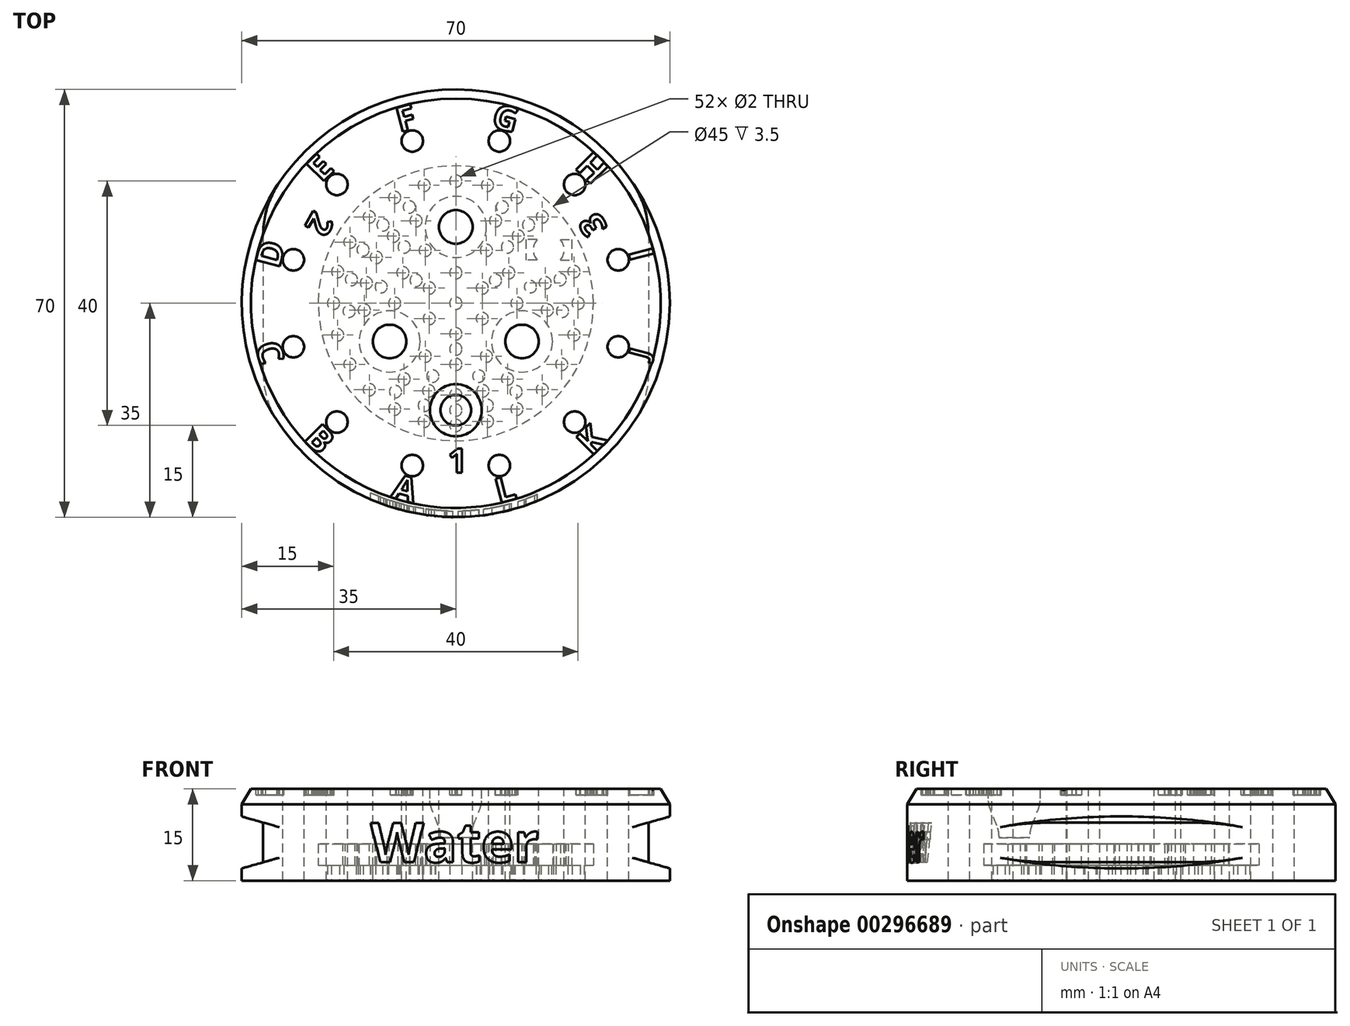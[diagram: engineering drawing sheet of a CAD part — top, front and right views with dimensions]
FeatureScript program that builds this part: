
annotation { "Feature Type Name" : "Feature", "Feature Type Description" : "" }
export const myFeature = defineFeature(function(context is Context, id is Id, definition is map)
    precondition{}
    {
        {
            var Q0;
            Q0=qCreatedBy(makeId("Top.planeOp"),FACE);
            var sketch = newSketch(context, id + "F0", { "sketchPlane" : qUnion([Q0])});
            skCircle(sketch, "E0", {"center": v(0, 0) * mm, "radius": 35 * mm});
            skSolve(sketch);
        }
        {
            var Q0;
            Q0=qSketchRegion(id+"F0",true);
            extrude(context, id + "F1", {"entities" : qUnion([Q0]), "depth" : 15 * mm});
        }
        {
            var Q0;
            Q0=qCreatedBy(makeId("Front.planeOp"),FACE);
            var sketch = newSketch(context, id + "F2", { "sketchPlane" : qUnion([Q0])});
            skText(sketch, "E1", { "text": "Water", "fontName": "OpenSans-Bold.ttf"});
            const initialGuessF2  = {"E1": [-0.01396, 0.003, 1, 0, 0.0065]};
            skSetInitialGuess(sketch, initialGuessF2);
            skSolve(sketch);
        }
        {
            var Q0;
            Q0=qSketchRegion(id+"F2",true);
            var Q1;
            Q1=makeQuery(id+"F1.opExtrude","SWEPT_FACE",FACE,{"disambiguationData":[OSD([sQuery(id+"F0.wireOp",EDGE,"E0")])]});
            extrude(context, id + "F3", {"entities" : qUnion([Q0]), "operationType" : NewBodyOperationType.REMOVE, "endBound" : BoundingType.THROUGH_ALL, "endBoundEntityFace" : qUnion([Q1]), "depth" : 25 * mm});
        }
        {
            var Q0;
            Q0=makeQuery(id+"F1.opExtrude","CAP_FACE",FACE,{"disambiguationData":[OSD([sQuery(id+"F0.wireOp",EDGE,"E0")])],"isStart":false});
            var sketch = newSketch(context, id + "F4", { "sketchPlane" : qUnion([Q0])});
            skCircle(sketch, "E2", {"center": v(0, 0) * mm, "radius": 34 * mm});
            skSolve(sketch);
        }
        {
            var Q0;
            Q0=qSketchRegion(id+"F4",true);
            var Q1;
            Q1=makeQuery(id+"F1.opExtrude","CAP_FACE",FACE,{"disambiguationData":[OSD([sQuery(id+"F0.wireOp",EDGE,"E0")])],"isStart":true});
            extrude(context, id + "F5", {"entities" : qUnion([Q0]), "operationType" : NewBodyOperationType.ADD, "endBound" : BoundingType.UP_TO_SURFACE, "oppositeDirection" : true, "endBoundEntityFace" : qUnion([Q1]), "depth" : 25 * mm});
        }
        {
            var Q0;
            Q0=qCreatedBy(makeId("Front.planeOp"),FACE);
            var sketch = newSketch(context, id + "F6", { "sketchPlane" : qUnion([Q0])});
            skLineSegment(sketch, "E3", {"start": v(-35, 10.5) * mm, "end": v(-35, 2) * mm});
            skLineSegment(sketch, "E4", {"start": v(-35, 2) * mm, "end": v(-31.5, 3) * mm});
            skLineSegment(sketch, "E5", {"start": v(-31.5, 3) * mm, "end": v(-31.5, 9.5) * mm});
            skLineSegment(sketch, "E6", {"start": v(-31.5, 9.5) * mm, "end": v(-35, 10.5) * mm});
            skLineSegment(sketch, "E7.MirrorCS", {"start": v(35, 10.5) * mm, "end": v(35, 2) * mm});
            skLineSegment(sketch, "E8.MirrorCS", {"start": v(31.5, 9.5) * mm, "end": v(35, 10.5) * mm});
            skLineSegment(sketch, "E9.MirrorCS", {"start": v(35, 2) * mm, "end": v(31.5, 3) * mm});
            skLineSegment(sketch, "E10.MirrorCS", {"start": v(31.5, 3) * mm, "end": v(31.5, 9.5) * mm});
            skSolve(sketch);
        }
        {
            var Q0;
            Q0=qSketchRegion(id+"F6",true);
            extrude(context, id + "F7", {"entities" : qUnion([Q0]), "operationType" : NewBodyOperationType.REMOVE, "endBound" : BoundingType.THROUGH_ALL, "oppositeDirection" : true, "depth" : 25 * mm, "hasSecondDirection" : true, "secondDirectionBound" : SecondDirectionBoundingType.THROUGH_ALL, "secondDirectionOppositeDirection" : false, "secondDirectionDepth" : 25 * mm});
        }
        {
            var Q0;
            {var subQ0=sQuery(id+"F0.wireOp",EDGE,"E0");Q0=makeQuery(id+"F7.boolean.opBoolean","INTERSECT",EDGE,{"disambiguationData":[OD(0.0)],"derivedFrom":[makeQuery(id+"F3.boolean.opBoolean","SPLIT",FACE,{"disambiguationData":[TD([makeQuery(id+"F1.opExtrude","CAP_FACE",FACE,{"disambiguationData":[OSD([subQ0])],"isStart":true})])],"derivedFrom":makeQuery(id+"F1.opExtrude","SWEPT_FACE",FACE,{"disambiguationData":[OSD([subQ0])]})}),makeQuery(id+"F7.opExtrude","SWEPT_FACE",FACE,{"disambiguationData":[OSD([sQuery(id+"F6.wireOp",EDGE,"E5")])]})]});}
            var Q1;
            {var subQ0=sQuery(id+"F0.wireOp",EDGE,"E0");Q1=makeQuery(id+"F7.boolean.opBoolean","INTERSECT",EDGE,{"disambiguationData":[OD(0.0)],"derivedFrom":[makeQuery(id+"F3.boolean.opBoolean","SPLIT",FACE,{"disambiguationData":[TD([makeQuery(id+"F1.opExtrude","CAP_FACE",FACE,{"disambiguationData":[OSD([subQ0])],"isStart":true})])],"derivedFrom":makeQuery(id+"F1.opExtrude","SWEPT_FACE",FACE,{"disambiguationData":[OSD([subQ0])]})}),makeQuery(id+"F7.opExtrude","SWEPT_FACE",FACE,{"disambiguationData":[OSD([sQuery(id+"F6.wireOp",EDGE,"E10.MirrorCS")])]})]});}
            var Q2;
            {var subQ0=sQuery(id+"F0.wireOp",EDGE,"E0");Q2=makeQuery(id+"F7.boolean.opBoolean","INTERSECT",EDGE,{"disambiguationData":[OD(1.0)],"derivedFrom":[makeQuery(id+"F3.boolean.opBoolean","SPLIT",FACE,{"disambiguationData":[TD([makeQuery(id+"F1.opExtrude","CAP_FACE",FACE,{"disambiguationData":[OSD([subQ0])],"isStart":true})])],"derivedFrom":makeQuery(id+"F1.opExtrude","SWEPT_FACE",FACE,{"disambiguationData":[OSD([subQ0])]})}),makeQuery(id+"F7.opExtrude","SWEPT_FACE",FACE,{"disambiguationData":[OSD([sQuery(id+"F6.wireOp",EDGE,"E10.MirrorCS")])]})]});}
            var Q3;
            {var subQ0=sQuery(id+"F0.wireOp",EDGE,"E0");Q3=makeQuery(id+"F7.boolean.opBoolean","INTERSECT",EDGE,{"disambiguationData":[OD(1.0)],"derivedFrom":[makeQuery(id+"F3.boolean.opBoolean","SPLIT",FACE,{"disambiguationData":[TD([makeQuery(id+"F1.opExtrude","CAP_FACE",FACE,{"disambiguationData":[OSD([subQ0])],"isStart":true})])],"derivedFrom":makeQuery(id+"F1.opExtrude","SWEPT_FACE",FACE,{"disambiguationData":[OSD([subQ0])]})}),makeQuery(id+"F7.opExtrude","SWEPT_FACE",FACE,{"disambiguationData":[OSD([sQuery(id+"F6.wireOp",EDGE,"E5")])]})]});}
            fillet(context, id + "F8", {"entities" : qUnion([Q0, Q1, Q2, Q3]), "radius" : 15 * mm, "tangentPropagation" : true, "allowEdgeOverflow" : false});
        }
        {
            var Q0;
            Q0=makeQuery(id+"F1.opExtrude","CAP_FACE",FACE,{"disambiguationData":[OSD([sQuery(id+"F0.wireOp",EDGE,"E0")])],"isStart":false});
            var sketch = newSketch(context, id + "F9", { "sketchPlane" : qUnion([Q0])});
            skCircle(sketch, "E11", {"center": v(0, 12.5) * mm, "radius": 2.75 * mm});
            skCircle(sketch, "E12.1.0", {"center": v(-10.83, -6.25) * mm, "radius": 2.75 * mm});
            skCircle(sketch, "E12.2.0", {"center": v(10.83, -6.25) * mm, "radius": 2.75 * mm});
            skPoint(sketch, "E12.center", {"position": v(0, 0) * mm});
            skCircle(sketch, "E13", {"center": v(0, 0) * mm, "radius": 12.5 * mm, "construction": true});
            skSolve(sketch);
        }
        {
            var Q0;
            Q0=qSketchRegion(id+"F9",true);
            extrude(context, id + "F10", {"entities" : qUnion([Q0]), "operationType" : NewBodyOperationType.REMOVE, "endBound" : BoundingType.THROUGH_ALL, "oppositeDirection" : true, "depth" : 25 * mm});
        }
        {
            var Q0;
            Q0=makeQuery(id+"F1.opExtrude","CAP_FACE",FACE,{"disambiguationData":[OSD([sQuery(id+"F0.wireOp",EDGE,"E0")])],"isStart":false});
            var sketch = newSketch(context, id + "F11", { "sketchPlane" : qUnion([Q0])});
            skCircle(sketch, "E14", {"center": v(0, -17.5) * mm, "radius": 2.5 * mm});
            skCircle(sketch, "E15", {"center": v(0, 0) * mm, "radius": 17.5 * mm, "construction": true});
            skSolve(sketch);
        }
        {
            var Q0;
            Q0=qSketchRegion(id+"F11",true);
            extrude(context, id + "F12", {"entities" : qUnion([Q0]), "operationType" : NewBodyOperationType.REMOVE, "endBound" : BoundingType.THROUGH_ALL, "oppositeDirection" : true, "depth" : 25 * mm});
        }
        {
            var Q0;
            Q0=makeQuery(id+"F1.opExtrude","CAP_FACE",FACE,{"disambiguationData":[OSD([sQuery(id+"F0.wireOp",EDGE,"E0")])],"isStart":false});
            var sketch = newSketch(context, id + "F13", { "sketchPlane" : qUnion([Q0])});
            skCircle(sketch, "E16", {"center": v(0, -17.5) * mm, "radius": 4.25 * mm});
            skSolve(sketch);
        }
        {
            var Q0;
            Q0=qSketchRegion(id+"F13",true);
            extrude(context, id + "F14", {"entities" : qUnion([Q0]), "operationType" : NewBodyOperationType.REMOVE, "oppositeDirection" : true, "depth" : 7.5 * mm});
        }
        {
            var Q0;
            Q0=makeQuery(id+"F14.boolean.opBoolean","COPY",EDGE,{"derivedFrom":makeQuery(id+"F14.opExtrude","CAP_EDGE",EDGE,{"disambiguationData":[OSD([sQuery(id+"F13.wireOp",EDGE,"E16")])],"isStart":false})});
            chamfer(context, id + "F15", {"entities" : qUnion([Q0]), "chamferType" : ChamferType.TWO_OFFSETS, "width1" : 5 * mm, "oppositeDirection" : true, "width2" : 2 * mm, "tangentPropagation" : true});
        }
        {
            var Q0;
            {var subQ0=sQuery(id+"F13.wireOp",EDGE,"E16");Q0=makeQuery(id+"F15.opChamfer","BLEND_EDGE",EDGE,{"blendedFrom":[makeQuery(id+"F14.boolean.opBoolean","COPY",EDGE,{"derivedFrom":makeQuery(id+"F14.opExtrude","CAP_EDGE",EDGE,{"disambiguationData":[OSD([subQ0])],"isStart":false})}),makeQuery(id+"F14.boolean.opBoolean","COPY",FACE,{"derivedFrom":makeQuery(id+"F14.opExtrude","SWEPT_FACE",FACE,{"disambiguationData":[OSD([subQ0])]})})],"blendedInto":[makeQuery(id+"F14.boolean.opBoolean","COPY",FACE,{"derivedFrom":makeQuery(id+"F14.opExtrude","SWEPT_FACE",FACE,{"disambiguationData":[OSD([subQ0])]})})]});}
            var Q1;
            Q1=makeQuery(id+"F15.opChamfer","BLEND_EDGE",EDGE,{"blendedFrom":[makeQuery(id+"F14.boolean.opBoolean","COPY",EDGE,{"derivedFrom":makeQuery(id+"F14.opExtrude","CAP_EDGE",EDGE,{"disambiguationData":[OSD([sQuery(id+"F13.wireOp",EDGE,"E16")])],"isStart":false})}),makeQuery(id+"F12.boolean.opBoolean","COPY",FACE,{"derivedFrom":makeQuery(id+"F12.opExtrude","SWEPT_FACE",FACE,{"disambiguationData":[OSD([sQuery(id+"F11.wireOp",EDGE,"E14")])]})})],"blendedInto":[makeQuery(id+"F12.boolean.opBoolean","COPY",FACE,{"derivedFrom":makeQuery(id+"F12.opExtrude","SWEPT_FACE",FACE,{"disambiguationData":[OSD([sQuery(id+"F11.wireOp",EDGE,"E14")])]})})]});
            fillet(context, id + "F16", {"entities" : qUnion([Q0, Q1]), "radius" : 5 * mm, "tangentPropagation" : true, "allowEdgeOverflow" : false});
        }
        {
            var Q0;
            Q0=makeQuery(id+"F1.opExtrude","CAP_FACE",FACE,{"disambiguationData":[OSD([sQuery(id+"F0.wireOp",EDGE,"E0")])],"isStart":false});
            var sketch = newSketch(context, id + "F17", { "sketchPlane" : qUnion([Q0])});
            skCircle(sketch, "E17", {"center": v(19.45, 19.45) * mm, "radius": 1.75 * mm});
            skCircle(sketch, "E18", {"center": v(0, 0) * mm, "radius": 27.5 * mm, "construction": true});
            skLineSegment(sketch, "E19", {"start": v(0, 0) * mm, "end": v(19.45, 19.45) * mm, "construction": true});
            skCircle(sketch, "E20.1.1", {"center": v(7.12, 26.56) * mm, "radius": 1.75 * mm});
            skCircle(sketch, "E20.2.1", {"center": v(-7.12, 26.56) * mm, "radius": 1.75 * mm});
            skCircle(sketch, "E20.3.1", {"center": v(-19.45, 19.45) * mm, "radius": 1.75 * mm});
            skCircle(sketch, "E20.4.1", {"center": v(-26.56, 7.12) * mm, "radius": 1.75 * mm});
            skCircle(sketch, "E20.5.1", {"center": v(-26.56, -7.12) * mm, "radius": 1.75 * mm});
            skCircle(sketch, "E20.6.1", {"center": v(-19.45, -19.45) * mm, "radius": 1.75 * mm});
            skCircle(sketch, "E20.7.1", {"center": v(-7.12, -26.56) * mm, "radius": 1.75 * mm});
            skCircle(sketch, "E20.8.1", {"center": v(7.12, -26.56) * mm, "radius": 1.75 * mm});
            skCircle(sketch, "E20.9.1", {"center": v(19.45, -19.45) * mm, "radius": 1.75 * mm});
            skCircle(sketch, "E20.10.1", {"center": v(26.56, -7.12) * mm, "radius": 1.75 * mm});
            skCircle(sketch, "E20.11.1", {"center": v(26.56, 7.12) * mm, "radius": 1.75 * mm});
            skSolve(sketch);
        }
        {
            var Q0;
            Q0=qSketchRegion(id+"F17",true);
            extrude(context, id + "F18", {"entities" : qUnion([Q0]), "operationType" : NewBodyOperationType.REMOVE, "endBound" : BoundingType.THROUGH_ALL, "oppositeDirection" : true, "depth" : 25 * mm});
        }
        {
            var Q0;
            Q0=makeQuery(id+"F1.opExtrude","CAP_EDGE",EDGE,{"disambiguationData":[OSD([sQuery(id+"F0.wireOp",EDGE,"E0")])],"isStart":false});
            chamfer(context, id + "F19", {"entities" : qUnion([Q0]), "chamferType" : ChamferType.TWO_OFFSETS, "width1" : 2.5 * mm, "oppositeDirection" : true, "width2" : 1.5 * mm, "tangentPropagation" : true});
        }
        {
            var Q0;
            Q0=makeQuery(id+"F1.opExtrude","CAP_FACE",FACE,{"disambiguationData":[OSD([sQuery(id+"F0.wireOp",EDGE,"E0")])],"isStart":false});
            var sketch = newSketch(context, id + "F20", { "sketchPlane" : qUnion([Q0])});
            skText(sketch, "E21", { "text": "A", "fontName": "OpenSans-Bold.ttf"});
            skText(sketch, "E22", { "text": "B", "fontName": "OpenSans-Bold.ttf"});
            skText(sketch, "E23", { "text": "C", "fontName": "OpenSans-Bold.ttf"});
            skText(sketch, "E24", { "text": "E", "fontName": "OpenSans-Bold.ttf"});
            skText(sketch, "E25", { "text": "F", "fontName": "OpenSans-Bold.ttf"});
            skText(sketch, "E26", { "text": "G", "fontName": "OpenSans-Bold.ttf"});
            skText(sketch, "E27", { "text": "H", "fontName": "OpenSans-Bold.ttf"});
            skText(sketch, "E28", { "text": "I", "fontName": "OpenSans-Bold.ttf"});
            skText(sketch, "E29", { "text": "J", "fontName": "OpenSans-Bold.ttf"});
            skText(sketch, "E30", { "text": "K", "fontName": "OpenSans-Bold.ttf"});
            skText(sketch, "E31", { "text": "L", "fontName": "OpenSans-Bold.ttf"});
            skText(sketch, "E32", { "text": "D", "fontName": "OpenSans-Bold.ttf"});
            skCircle(sketch, "E33", {"center": v(0, 0) * mm, "radius": 29.38 * mm, "construction": true});
            skText(sketch, "E34", { "text": "1", "fontName": "OpenSans-Bold.ttf"});
            skText(sketch, "E35", { "text": "2", "fontName": "OpenSans-Bold.ttf"});
            skText(sketch, "E36", { "text": "3", "fontName": "OpenSans-Bold.ttf"});
            skCircle(sketch, "E37", {"center": v(0, 0) * mm, "radius": 23.75 * mm, "construction": true});
            const initialGuessF20  = {"E21": [-0.0107, -0.03174, 0.96593, -0.25882, 0.00406], "E22": [-0.025, -0.02228, 0.7071, -0.7071, 0.00406], "E23": [-0.03278, -0.00684, 0.25882, -0.96593, 0.00406], "E24": [-0.0219, 0.01964, 0.7071, 0.7071, 0.00406], "E25": [-0.00914, 0.02796, 0.96593, 0.25882, 0.00406], "E26": [0.00567, 0.0289, 0.96593, -0.25882, 0.00406], "E27": [0.0193, 0.02225, 0.7071, -0.7071, 0.00406], "E28": [0.02815, 0.00844, 0.25882, -0.96593, 0.00406], "E29": [0.0313, -0.00927, 0.25882, 0.96593, 0.00325], "E30": [0.02219, -0.0251, 0.7071, 0.7071, 0.00406], "E31": [0.00703, -0.03273, 0.96593, 0.25882, 0.00406], "E32": [-0.02892, 0.00557, 0.25882, 0.96593, 0.00406], "E34": [-0.00133, -0.02775, 1, 0, 0.004], "E35": [-0.0232, 0.01533, -0.5, -0.86603, 0.004], "E36": [0.02486, 0.01244, -0.5, 0.86603, 0.004]};
            skSetInitialGuess(sketch, initialGuessF20);
            skSolve(sketch);
        }
        {
            var Q0;
            Q0=qSketchRegion(id+"F20",true);
            extrude(context, id + "F21", {"entities" : qUnion([Q0]), "operationType" : NewBodyOperationType.REMOVE, "oppositeDirection" : true, "depth" : 1 * mm});
        }
        {
            var Q0;
            Q0=makeQuery(id+"F1.opExtrude","CAP_FACE",FACE,{"disambiguationData":[OSD([sQuery(id+"F0.wireOp",EDGE,"E0")])],"isStart":true});
            var sketch = newSketch(context, id + "F22", { "sketchPlane" : qUnion([Q0])});
            skCircle(sketch, "E38.0", {"center": v(0, 17.5) * mm, "radius": 2.5 * mm});
            skCircle(sketch, "E38.1", {"center": v(-15.16, -8.75) * mm, "radius": 2.5 * mm});
            skSolve(sketch);
        }
        {
            var Q0;
            Q0=qSketchRegion(id+"F22",true);
            extrude(context, id + "F23", {"entities" : qUnion([Q0]), "operationType" : NewBodyOperationType.ADD, "oppositeDirection" : true, "depth" : 7 * mm});
        }
        {
            var Q0;
            Q0=makeQuery(id+"F23.boolean.opBoolean","MERGE",FACE,{"derivedFrom":[makeQuery(id+"F1.opExtrude","CAP_FACE",FACE,{"disambiguationData":[OSD([sQuery(id+"F0.wireOp",EDGE,"E0")])],"isStart":true}),makeQuery(id+"F23.opExtrude","CAP_FACE",FACE,{"disambiguationData":[OSD([sQuery(id+"F22.wireOp",EDGE,"E38.0")])],"isStart":true}),makeQuery(id+"F23.opExtrude","CAP_FACE",FACE,{"disambiguationData":[OSD([sQuery(id+"F22.wireOp",EDGE,"E38.1")])],"isStart":true})]});
            var sketch = newSketch(context, id + "F24", { "sketchPlane" : qUnion([Q0])});
            skCircle(sketch, "E39", {"center": v(0, 0) * mm, "radius": 22.5 * mm});
            skCircle(sketch, "E40", {"center": v(10.83, 6.25) * mm, "radius": 5 * mm});
            skCircle(sketch, "E41", {"center": v(-10.83, 6.25) * mm, "radius": 5 * mm});
            skCircle(sketch, "E42", {"center": v(0, -12.5) * mm, "radius": 5 * mm});
            skSolve(sketch);
        }
        {
            var Q0;
            Q0=qSketchRegion(id+"F24",true);
            extrude(context, id + "F25", {"entities" : qUnion([Q0]), "operationType" : NewBodyOperationType.REMOVE, "oppositeDirection" : true, "depth" : 6 * mm});
        }
        {
            var Q0;
            Q0=makeQuery(id+"F25.boolean.opBoolean","COPY",FACE,{"derivedFrom":makeQuery(id+"F25.opExtrude","CAP_FACE",FACE,{"disambiguationData":[OSD([sQuery(id+"F24.wireOp",EDGE,"E39"),sQuery(id+"F24.wireOp",EDGE,"E40"),sQuery(id+"F24.wireOp",EDGE,"E41"),sQuery(id+"F24.wireOp",EDGE,"E42")])],"isStart":false})});
            var sketch = newSketch(context, id + "F26", { "sketchPlane" : qUnion([Q0])});
            skCircle(sketch, "E43", {"center": v(0, 0) * mm, "radius": 1 * mm});
            skCircle(sketch, "E44", {"center": v(0, 7.5) * mm, "radius": 1 * mm});
            skCircle(sketch, "E45", {"center": v(3.76, 11.92) * mm, "radius": 1 * mm});
            skCircle(sketch, "E46", {"center": v(-3.76, 11.92) * mm, "radius": 1 * mm});
            skCircle(sketch, "E47", {"center": v(0, 17.5) * mm, "radius": 1 * mm});
            skLineSegment(sketch, "E48", {"start": v(3.76, 11.92) * mm, "end": v(0, 0) * mm, "construction": true});
            skCircle(sketch, "E49.1.0", {"center": v(-6.5, -3.75) * mm, "radius": 1 * mm});
            skCircle(sketch, "E49.1.1", {"center": v(-8.44, -9.22) * mm, "radius": 1 * mm});
            skCircle(sketch, "E49.1.2", {"center": v(-12.2, -2.7) * mm, "radius": 1 * mm});
            skCircle(sketch, "E49.2.0", {"center": v(6.5, -3.75) * mm, "radius": 1 * mm});
            skCircle(sketch, "E49.2.1", {"center": v(12.2, -2.7) * mm, "radius": 1 * mm});
            skCircle(sketch, "E49.2.2", {"center": v(8.44, -9.22) * mm, "radius": 1 * mm});
            skCircle(sketch, "E50.1.0", {"center": v(-5.16, 16.72) * mm, "radius": 1 * mm});
            skCircle(sketch, "E50.2.0", {"center": v(-9.86, 14.46) * mm, "radius": 1 * mm});
            skCircle(sketch, "E50.5.0", {"center": v(-17.45, 1.3) * mm, "radius": 1 * mm});
            skCircle(sketch, "E50.6.0", {"center": v(-17.06, -3.9) * mm, "radius": 1 * mm});
            skCircle(sketch, "E50.7.0", {"center": v(-15.16, -8.75) * mm, "radius": 1 * mm});
            skCircle(sketch, "E50.8.0", {"center": v(-11.9, -12.83) * mm, "radius": 1 * mm});
            skCircle(sketch, "E50.9.0", {"center": v(-7.6, -15.77) * mm, "radius": 1 * mm});
            skCircle(sketch, "E50.12.0", {"center": v(7.6, -15.77) * mm, "radius": 1 * mm});
            skCircle(sketch, "E50.13.0", {"center": v(11.9, -12.83) * mm, "radius": 1 * mm});
            skCircle(sketch, "E50.15.0", {"center": v(17.06, -3.9) * mm, "radius": 1 * mm});
            skCircle(sketch, "E50.16.0", {"center": v(17.45, 1.3) * mm, "radius": 1 * mm});
            skCircle(sketch, "E50.19.0", {"center": v(9.86, 14.46) * mm, "radius": 1 * mm});
            skCircle(sketch, "E50.20.0", {"center": v(5.16, 16.72) * mm, "radius": 1 * mm});
            skSolve(sketch);
        }
        {
            var Q0;
            Q0=qSketchRegion(id+"F26",true);
            var Q1;
            {var subQ0=sQuery(id+"F0.wireOp",EDGE,"E0");Q1=makeQuery(id+"F25.boolean.opBoolean","SPLIT",FACE,{"disambiguationData":[TD([makeQuery(id+"F1.opExtrude","SWEPT_FACE",FACE,{"disambiguationData":[OSD([subQ0])]})])],"derivedFrom":makeQuery(id+"F23.boolean.opBoolean","MERGE",FACE,{"derivedFrom":[makeQuery(id+"F1.opExtrude","CAP_FACE",FACE,{"disambiguationData":[OSD([subQ0])],"isStart":true}),makeQuery(id+"F23.opExtrude","CAP_FACE",FACE,{"disambiguationData":[OSD([sQuery(id+"F22.wireOp",EDGE,"E38.0")])],"isStart":true}),makeQuery(id+"F23.opExtrude","CAP_FACE",FACE,{"disambiguationData":[OSD([sQuery(id+"F22.wireOp",EDGE,"E38.1")])],"isStart":true})]})});}
            extrude(context, id + "F27", {"entities" : qUnion([Q0]), "operationType" : NewBodyOperationType.ADD, "endBound" : BoundingType.UP_TO_SURFACE, "endBoundEntityFace" : qUnion([Q1]), "depth" : 25 * mm});
        }
        {
            var Q0;
            {var subQ0=sQuery(id+"F0.wireOp",EDGE,"E0");Q0=makeQuery(id+"F25.boolean.opBoolean","SPLIT",FACE,{"disambiguationData":[TD([makeQuery(id+"F1.opExtrude","SWEPT_FACE",FACE,{"disambiguationData":[OSD([subQ0])]})])],"derivedFrom":makeQuery(id+"F23.boolean.opBoolean","MERGE",FACE,{"derivedFrom":[makeQuery(id+"F1.opExtrude","CAP_FACE",FACE,{"disambiguationData":[OSD([subQ0])],"isStart":true}),makeQuery(id+"F23.opExtrude","CAP_FACE",FACE,{"disambiguationData":[OSD([sQuery(id+"F22.wireOp",EDGE,"E38.0")])],"isStart":true}),makeQuery(id+"F23.opExtrude","CAP_FACE",FACE,{"disambiguationData":[OSD([sQuery(id+"F22.wireOp",EDGE,"E38.1")])],"isStart":true})]})});}
            var sketch = newSketch(context, id + "F28", { "sketchPlane" : qUnion([Q0])});
            skCircle(sketch, "E51.0", {"center": v(0, 0) * mm, "radius": 22.5 * mm});
            skCircle(sketch, "E52.0", {"center": v(-10.83, 6.25) * mm, "radius": 2.75 * mm});
            skCircle(sketch, "E52.1", {"center": v(10.83, 6.25) * mm, "radius": 2.75 * mm});
            skCircle(sketch, "E52.2", {"center": v(0, -12.5) * mm, "radius": 2.75 * mm});
            skSolve(sketch);
        }
        {
            var Q0;
            Q0=qSketchRegion(id+"F28",true);
            extrude(context, id + "F29", {"entities" : qUnion([Q0]), "operationType" : NewBodyOperationType.ADD, "oppositeDirection" : true, "depth" : 2.5 * mm});
        }
        {
            var Q0;
            {var subQ0=sQuery(id+"F0.wireOp",EDGE,"E0");var subQ1=makeQuery(id+"F23.boolean.opBoolean","MERGE",FACE,{"derivedFrom":[makeQuery(id+"F1.opExtrude","CAP_FACE",FACE,{"disambiguationData":[OSD([subQ0])],"isStart":true}),makeQuery(id+"F23.opExtrude","CAP_FACE",FACE,{"disambiguationData":[OSD([sQuery(id+"F22.wireOp",EDGE,"E38.0")])],"isStart":true}),makeQuery(id+"F23.opExtrude","CAP_FACE",FACE,{"disambiguationData":[OSD([sQuery(id+"F22.wireOp",EDGE,"E38.1")])],"isStart":true})]});Q0=makeQuery(id+"F29.boolean.opBoolean","MERGE",FACE,{"derivedFrom":[makeQuery(id+"F25.boolean.opBoolean","SPLIT",FACE,{"disambiguationData":[TD([makeQuery(id+"F1.opExtrude","SWEPT_FACE",FACE,{"disambiguationData":[OSD([subQ0])]})])],"derivedFrom":subQ1}),makeQuery(id+"F25.boolean.opBoolean","SPLIT",FACE,{"disambiguationData":[TD([makeQuery(id+"F10.boolean.opBoolean","COPY",FACE,{"derivedFrom":makeQuery(id+"F10.opExtrude","SWEPT_FACE",FACE,{"disambiguationData":[OSD([sQuery(id+"F9.wireOp",EDGE,"E11")])]})})])],"derivedFrom":subQ1}),makeQuery(id+"F25.boolean.opBoolean","SPLIT",FACE,{"disambiguationData":[TD([makeQuery(id+"F10.boolean.opBoolean","COPY",FACE,{"derivedFrom":makeQuery(id+"F10.opExtrude","SWEPT_FACE",FACE,{"disambiguationData":[OSD([sQuery(id+"F9.wireOp",EDGE,"E12.1.0")])]})})])],"derivedFrom":subQ1}),makeQuery(id+"F25.boolean.opBoolean","SPLIT",FACE,{"disambiguationData":[TD([makeQuery(id+"F10.boolean.opBoolean","COPY",FACE,{"derivedFrom":makeQuery(id+"F10.opExtrude","SWEPT_FACE",FACE,{"disambiguationData":[OSD([sQuery(id+"F9.wireOp",EDGE,"E12.2.0")])]})})])],"derivedFrom":subQ1}),makeQuery(id+"F27.opExtrude","CAP_FACE",FACE,{"disambiguationData":[OSD([sQuery(id+"F26.wireOp",EDGE,"E43")])],"isStart":false}),makeQuery(id+"F27.opExtrude","CAP_FACE",FACE,{"disambiguationData":[OSD([sQuery(id+"F26.wireOp",EDGE,"E44")])],"isStart":false}),makeQuery(id+"F27.opExtrude","CAP_FACE",FACE,{"disambiguationData":[OSD([sQuery(id+"F26.wireOp",EDGE,"E45")])],"isStart":false}),makeQuery(id+"F27.opExtrude","CAP_FACE",FACE,{"disambiguationData":[OSD([sQuery(id+"F26.wireOp",EDGE,"E46")])],"isStart":false}),makeQuery(id+"F27.opExtrude","CAP_FACE",FACE,{"disambiguationData":[OSD([sQuery(id+"F26.wireOp",EDGE,"E47")])],"isStart":false}),makeQuery(id+"F27.opExtrude","CAP_FACE",FACE,{"disambiguationData":[OSD([sQuery(id+"F26.wireOp",EDGE,"E49.1.0")])],"isStart":false}),makeQuery(id+"F27.opExtrude","CAP_FACE",FACE,{"disambiguationData":[OSD([sQuery(id+"F26.wireOp",EDGE,"E49.1.1")])],"isStart":false}),makeQuery(id+"F27.opExtrude","CAP_FACE",FACE,{"disambiguationData":[OSD([sQuery(id+"F26.wireOp",EDGE,"E49.1.2")])],"isStart":false}),makeQuery(id+"F27.opExtrude","CAP_FACE",FACE,{"disambiguationData":[OSD([sQuery(id+"F26.wireOp",EDGE,"E49.2.0")])],"isStart":false}),makeQuery(id+"F27.opExtrude","CAP_FACE",FACE,{"disambiguationData":[OSD([sQuery(id+"F26.wireOp",EDGE,"E49.2.1")])],"isStart":false}),makeQuery(id+"F27.opExtrude","CAP_FACE",FACE,{"disambiguationData":[OSD([sQuery(id+"F26.wireOp",EDGE,"E49.2.2")])],"isStart":false}),makeQuery(id+"F27.opExtrude","CAP_FACE",FACE,{"disambiguationData":[OSD([sQuery(id+"F26.wireOp",EDGE,"E50.1.0")])],"isStart":false}),makeQuery(id+"F27.opExtrude","CAP_FACE",FACE,{"disambiguationData":[OSD([sQuery(id+"F26.wireOp",EDGE,"E50.2.0")])],"isStart":false}),makeQuery(id+"F27.opExtrude","CAP_FACE",FACE,{"disambiguationData":[OSD([sQuery(id+"F26.wireOp",EDGE,"E50.5.0")])],"isStart":false}),makeQuery(id+"F27.opExtrude","CAP_FACE",FACE,{"disambiguationData":[OSD([sQuery(id+"F26.wireOp",EDGE,"E50.6.0")])],"isStart":false}),makeQuery(id+"F27.opExtrude","CAP_FACE",FACE,{"disambiguationData":[OSD([sQuery(id+"F26.wireOp",EDGE,"E50.7.0")])],"isStart":false}),makeQuery(id+"F27.opExtrude","CAP_FACE",FACE,{"disambiguationData":[OSD([sQuery(id+"F26.wireOp",EDGE,"E50.8.0")])],"isStart":false}),makeQuery(id+"F27.opExtrude","CAP_FACE",FACE,{"disambiguationData":[OSD([sQuery(id+"F26.wireOp",EDGE,"E50.9.0")])],"isStart":false}),makeQuery(id+"F27.opExtrude","CAP_FACE",FACE,{"disambiguationData":[OSD([sQuery(id+"F26.wireOp",EDGE,"E50.12.0")])],"isStart":false}),makeQuery(id+"F27.opExtrude","CAP_FACE",FACE,{"disambiguationData":[OSD([sQuery(id+"F26.wireOp",EDGE,"E50.13.0")])],"isStart":false}),makeQuery(id+"F27.opExtrude","CAP_FACE",FACE,{"disambiguationData":[OSD([sQuery(id+"F26.wireOp",EDGE,"E50.15.0")])],"isStart":false}),makeQuery(id+"F27.opExtrude","CAP_FACE",FACE,{"disambiguationData":[OSD([sQuery(id+"F26.wireOp",EDGE,"E50.16.0")])],"isStart":false}),makeQuery(id+"F27.opExtrude","CAP_FACE",FACE,{"disambiguationData":[OSD([sQuery(id+"F26.wireOp",EDGE,"E50.19.0")])],"isStart":false}),makeQuery(id+"F27.opExtrude","CAP_FACE",FACE,{"disambiguationData":[OSD([sQuery(id+"F26.wireOp",EDGE,"E50.20.0")])],"isStart":false}),makeQuery(id+"F29.opExtrude","CAP_FACE",FACE,{"disambiguationData":[OSD([sQuery(id+"F28.wireOp",EDGE,"E51.0")])],"isStart":true})]});}
            var sketch = newSketch(context, id + "F30", { "sketchPlane" : qUnion([Q0])});
            skCircle(sketch, "E53", {"center": v(0, 5) * mm, "radius": 1 * mm});
            skCircle(sketch, "E54.0.1.0", {"center": v(0, 10) * mm, "radius": 1 * mm});
            skCircle(sketch, "E54.0.2.0", {"center": v(0, 15) * mm, "radius": 1 * mm});
            skCircle(sketch, "E54.0.3.0", {"center": v(0, 20) * mm, "radius": 1 * mm});
            skLineSegment(sketch, "E54.direction1", {"start": v(0, 5) * mm, "end": v(25, 5) * mm, "construction": true});
            skLineSegment(sketch, "E54.direction2", {"start": v(0, 5) * mm, "end": v(0, 10) * mm, "construction": true});
            skCircle(sketch, "E55.1.0", {"center": v(-4.33, 2.5) * mm, "radius": 1 * mm});
            skCircle(sketch, "E55.2.0", {"center": v(-4.33, -2.5) * mm, "radius": 1 * mm});
            skCircle(sketch, "E55.3.0", {"center": v(0, -5) * mm, "radius": 1 * mm});
            skCircle(sketch, "E55.4.0", {"center": v(4.33, -2.5) * mm, "radius": 1 * mm});
            skCircle(sketch, "E55.5.0", {"center": v(4.33, 2.5) * mm, "radius": 1 * mm});
            skPoint(sketch, "E55.center", {"position": v(0, 0) * mm});
            skCircle(sketch, "E56.1.0", {"center": v(-5, 8.66) * mm, "radius": 1 * mm});
            skCircle(sketch, "E56.3.0", {"center": v(-10, 0) * mm, "radius": 1 * mm});
            skCircle(sketch, "E56.4.0", {"center": v(-8.66, -5) * mm, "radius": 1 * mm});
            skCircle(sketch, "E56.5.0", {"center": v(-5, -8.66) * mm, "radius": 1 * mm});
            skCircle(sketch, "E56.7.0", {"center": v(5, -8.66) * mm, "radius": 1 * mm});
            skCircle(sketch, "E56.8.0", {"center": v(8.66, -5) * mm, "radius": 1 * mm});
            skCircle(sketch, "E56.9.0", {"center": v(10, 0) * mm, "radius": 1 * mm});
            skCircle(sketch, "E56.11.0", {"center": v(5, 8.66) * mm, "radius": 1 * mm});
            skCircle(sketch, "E57.1.0", {"center": v(-4.42, 14.33) * mm, "radius": 1 * mm});
            skCircle(sketch, "E57.2.0", {"center": v(-8.45, 12.4) * mm, "radius": 1 * mm});
            skCircle(sketch, "E57.5.0", {"center": v(-14.96, 1.12) * mm, "radius": 1 * mm});
            skCircle(sketch, "E57.6.0", {"center": v(-14.62, -3.34) * mm, "radius": 1 * mm});
            skCircle(sketch, "E57.7.0", {"center": v(-13, -7.5) * mm, "radius": 1 * mm});
            skCircle(sketch, "E57.8.0", {"center": v(-10.2, -11) * mm, "radius": 1 * mm});
            skCircle(sketch, "E57.9.0", {"center": v(-6.5, -13.51) * mm, "radius": 1 * mm});
            skCircle(sketch, "E57.12.0", {"center": v(6.5, -13.51) * mm, "radius": 1 * mm});
            skCircle(sketch, "E57.13.0", {"center": v(10.2, -11) * mm, "radius": 1 * mm});
            skCircle(sketch, "E57.15.0", {"center": v(14.62, -3.34) * mm, "radius": 1 * mm});
            skCircle(sketch, "E57.16.0", {"center": v(14.96, 1.12) * mm, "radius": 1 * mm});
            skCircle(sketch, "E57.19.0", {"center": v(8.45, 12.4) * mm, "radius": 1 * mm});
            skCircle(sketch, "E57.20.0", {"center": v(4.42, 14.33) * mm, "radius": 1 * mm});
            skCircle(sketch, "E58.1.0", {"center": v(-5.18, 19.32) * mm, "radius": 1 * mm});
            skCircle(sketch, "E58.2.0", {"center": v(-10, 17.32) * mm, "radius": 1 * mm});
            skCircle(sketch, "E58.3.0", {"center": v(-14.14, 14.14) * mm, "radius": 1 * mm});
            skCircle(sketch, "E58.4.0", {"center": v(-17.32, 10) * mm, "radius": 1 * mm});
            skCircle(sketch, "E58.5.0", {"center": v(-19.32, 5.18) * mm, "radius": 1 * mm});
            skCircle(sketch, "E58.6.0", {"center": v(-20, 0) * mm, "radius": 1 * mm});
            skCircle(sketch, "E58.7.0", {"center": v(-19.32, -5.18) * mm, "radius": 1 * mm});
            skCircle(sketch, "E58.8.0", {"center": v(-17.32, -10) * mm, "radius": 1 * mm});
            skCircle(sketch, "E58.9.0", {"center": v(-14.14, -14.14) * mm, "radius": 1 * mm});
            skCircle(sketch, "E58.10.0", {"center": v(-10, -17.32) * mm, "radius": 1 * mm});
            skCircle(sketch, "E58.11.0", {"center": v(-5.18, -19.32) * mm, "radius": 1 * mm});
            skCircle(sketch, "E58.12.0", {"center": v(0, -20) * mm, "radius": 1 * mm});
            skCircle(sketch, "E58.13.0", {"center": v(5.18, -19.32) * mm, "radius": 1 * mm});
            skCircle(sketch, "E58.14.0", {"center": v(10, -17.32) * mm, "radius": 1 * mm});
            skCircle(sketch, "E58.15.0", {"center": v(14.14, -14.14) * mm, "radius": 1 * mm});
            skCircle(sketch, "E58.17.0", {"center": v(19.32, -5.18) * mm, "radius": 1 * mm});
            skCircle(sketch, "E58.18.0", {"center": v(20, 0) * mm, "radius": 1 * mm});
            skCircle(sketch, "E58.19.0", {"center": v(19.32, 5.18) * mm, "radius": 1 * mm});
            skCircle(sketch, "E58.20.0", {"center": v(17.32, 10) * mm, "radius": 1 * mm});
            skCircle(sketch, "E58.21.0", {"center": v(14.14, 14.14) * mm, "radius": 1 * mm});
            skCircle(sketch, "E58.22.0", {"center": v(10, 17.32) * mm, "radius": 1 * mm});
            skCircle(sketch, "E58.23.0", {"center": v(5.18, 19.32) * mm, "radius": 1 * mm});
            skSolve(sketch);
        }
        {
            var Q0;
            Q0=qSketchRegion(id+"F30",true);
            extrude(context, id + "F31", {"entities" : qUnion([Q0]), "operationType" : NewBodyOperationType.REMOVE, "endBound" : BoundingType.UP_TO_NEXT, "oppositeDirection" : true, "depth" : 25 * mm});
        }
        {
            var Q0;
            Q0=makeQuery(id+"F29.opExtrude","CAP_FACE",FACE,{"disambiguationData":[OSD([sQuery(id+"F28.wireOp",EDGE,"E51.0"),sQuery(id+"F28.wireOp",EDGE,"E52.0"),sQuery(id+"F28.wireOp",EDGE,"E52.1"),sQuery(id+"F28.wireOp",EDGE,"E52.2")])],"isStart":false});
            var sketch = newSketch(context, id + "F32", { "sketchPlane" : qUnion([Q0])});
            skLineSegment(sketch, "E59.bottom", {"start": v(13.3, 10.44) * mm, "end": v(11.45, 10.44) * mm});
            skLineSegment(sketch, "E59.top", {"start": v(13.3, 7.08) * mm, "end": v(11.45, 7.08) * mm});
            skLineSegment(sketch, "E59.right", {"start": v(11.45, 10.44) * mm, "end": v(11.45, 7.08) * mm});
            skArc(sketch, "E60", {"start": v(13.3, 10.44) * mm, "mid": v(12.67, 8.76) * mm, "end": v(13.3, 7.08) * mm});
            skLineSegment(sketch, "E61", {"start": v(15.2, 8.76) * mm, "end": v(15.2, 10.37) * mm});
            skLineSegment(sketch, "E62.MirrorCS", {"start": v(18.94, 10.44) * mm, "end": v(18.94, 7.08) * mm});
            skArc(sketch, "E63.MirrorCS", {"start": v(17.08, 10.44) * mm, "mid": v(17.72, 8.76) * mm, "end": v(17.08, 7.08) * mm});
            skLineSegment(sketch, "E64.MirrorCS", {"start": v(17.08, 10.44) * mm, "end": v(18.94, 10.44) * mm});
            skLineSegment(sketch, "E65.MirrorCS", {"start": v(17.08, 7.08) * mm, "end": v(18.94, 7.08) * mm});
            skSolve(sketch);
        }
        {
            var Q0;
            Q0 = qSketchRegion(id + "F32", true);
            extrude(context, id + "F33", {"entities" : qUnion([Q0]), "operationType" : NewBodyOperationType.ADD, "depth" : 4.5 * mm});
        }
    });
